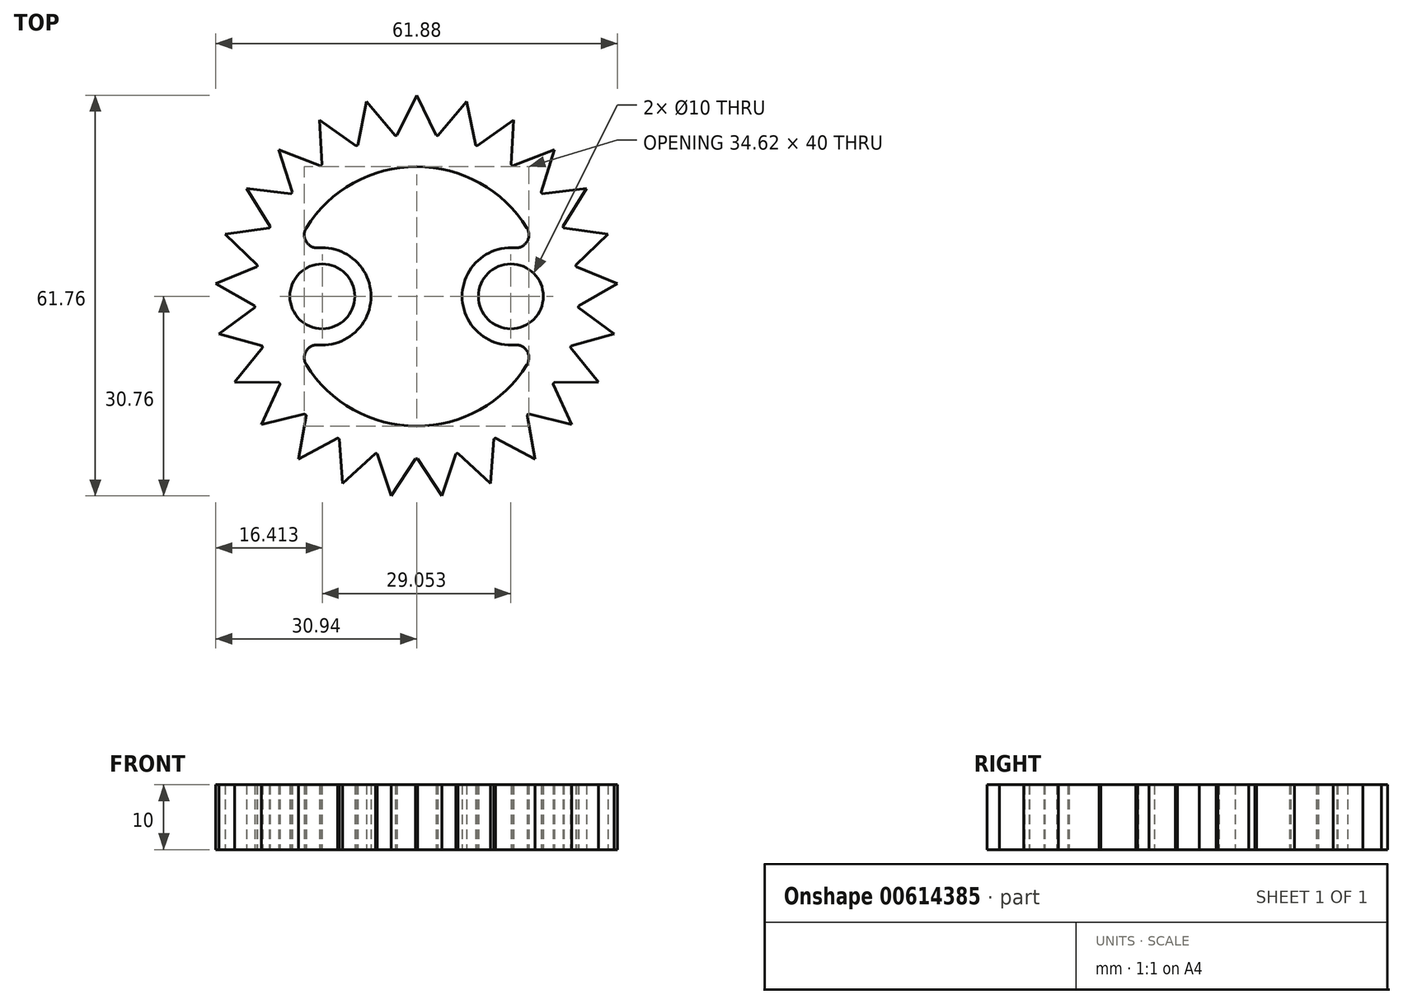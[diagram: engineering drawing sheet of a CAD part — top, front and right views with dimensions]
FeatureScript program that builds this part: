
annotation { "Feature Type Name" : "Feature", "Feature Type Description" : "" }
export const myFeature = defineFeature(function(context is Context, id is Id, definition is map)
    precondition{}
    {
        {
            var Q0;
            Q0=qCreatedBy(makeId("Top.planeOp"),FACE);
            var sketch = newSketch(context, id + "F0", { "sketchPlane" : qUnion([Q0])});
            skArc(sketch, "E0", {"start": v(-17, -10.52) * mm, "mid": v(0, -20) * mm, "end": v(17, -10.52) * mm});
            skArc(sketch, "E1", {"start": v(-14.59, 20.3) * mm, "mid": v(-14.7, 20.23) * mm, "end": v(-14.8, 20.15) * mm});
            skLineSegment(sketch, "E2", {"start": v(3, 24.82) * mm, "end": v(0, 31) * mm});
            skLineSegment(sketch, "E3", {"start": v(-3, 24.82) * mm, "end": v(0, 31) * mm});
            skLineSegment(sketch, "E4.1.0", {"start": v(-3.27, 24.79) * mm, "end": v(-7.7, 30.03) * mm});
            skLineSegment(sketch, "E4.1.1", {"start": v(-9.08, 23.3) * mm, "end": v(-7.7, 30.03) * mm});
            skLineSegment(sketch, "E4.2.0", {"start": v(-9.33, 23.2) * mm, "end": v(-14.93, 27.17) * mm});
            skLineSegment(sketch, "E4.2.1", {"start": v(-14.59, 20.3) * mm, "end": v(-14.93, 27.17) * mm});
            skLineSegment(sketch, "E4.3.0", {"start": v(-14.8, 20.15) * mm, "end": v(-21.22, 22.6) * mm});
            skLineSegment(sketch, "E4.3.1", {"start": v(-19.18, 16.04) * mm, "end": v(-21.22, 22.6) * mm});
            skLineSegment(sketch, "E4.4.0", {"start": v(-19.35, 15.83) * mm, "end": v(-26.17, 16.61) * mm});
            skLineSegment(sketch, "E4.4.1", {"start": v(-22.56, 10.77) * mm, "end": v(-26.17, 16.61) * mm});
            skLineSegment(sketch, "E4.5.0", {"start": v(-22.68, 10.52) * mm, "end": v(-29.48, 9.58) * mm});
            skLineSegment(sketch, "E4.5.1", {"start": v(-24.53, 4.82) * mm, "end": v(-29.48, 9.58) * mm});
            skLineSegment(sketch, "E4.6.0", {"start": v(-24.58, 4.55) * mm, "end": v(-30.94, 1.95) * mm});
            skLineSegment(sketch, "E4.6.1", {"start": v(-24.96, -1.44) * mm, "end": v(-30.94, 1.95) * mm});
            skLineSegment(sketch, "E4.7.0", {"start": v(-24.94, -1.7) * mm, "end": v(-30.45, -5.8) * mm});
            skLineSegment(sketch, "E4.7.1", {"start": v(-23.82, -7.6) * mm, "end": v(-30.45, -5.8) * mm});
            skLineSegment(sketch, "E4.8.0", {"start": v(-23.73, -7.85) * mm, "end": v(-28.05, -13.2) * mm});
            skLineSegment(sketch, "E4.8.1", {"start": v(-21.18, -13.28) * mm, "end": v(-28.05, -13.2) * mm});
            skLineSegment(sketch, "E4.9.0", {"start": v(-21.04, -13.5) * mm, "end": v(-23.89, -19.76) * mm});
            skLineSegment(sketch, "E4.9.1", {"start": v(-17.21, -18.13) * mm, "end": v(-23.89, -19.76) * mm});
            skLineSegment(sketch, "E4.10.0", {"start": v(-17.02, -18.32) * mm, "end": v(-18.22, -25.08) * mm});
            skLineSegment(sketch, "E4.10.1", {"start": v(-12.16, -21.84) * mm, "end": v(-18.22, -25.08) * mm});
            skLineSegment(sketch, "E4.11.0", {"start": v(-11.93, -21.97) * mm, "end": v(-11.41, -28.82) * mm});
            skLineSegment(sketch, "E4.11.1", {"start": v(-6.35, -24.18) * mm, "end": v(-11.41, -28.82) * mm});
            skLineSegment(sketch, "E4.12.0", {"start": v(-6.09, -24.25) * mm, "end": v(-3.89, -30.76) * mm});
            skLineSegment(sketch, "E4.12.1", {"start": v(-0.13, -25) * mm, "end": v(-3.89, -30.76) * mm});
            skLineSegment(sketch, "E4.13.0", {"start": v(0.13, -25) * mm, "end": v(3.89, -30.76) * mm});
            skLineSegment(sketch, "E4.13.1", {"start": v(6.09, -24.25) * mm, "end": v(3.89, -30.76) * mm});
            skLineSegment(sketch, "E4.14.0", {"start": v(6.35, -24.18) * mm, "end": v(11.41, -28.82) * mm});
            skLineSegment(sketch, "E4.14.1", {"start": v(11.93, -21.97) * mm, "end": v(11.41, -28.82) * mm});
            skLineSegment(sketch, "E4.15.0", {"start": v(12.16, -21.84) * mm, "end": v(18.22, -25.08) * mm});
            skLineSegment(sketch, "E4.15.1", {"start": v(17.02, -18.32) * mm, "end": v(18.22, -25.08) * mm});
            skLineSegment(sketch, "E4.16.0", {"start": v(17.21, -18.13) * mm, "end": v(23.89, -19.76) * mm});
            skLineSegment(sketch, "E4.16.1", {"start": v(21.04, -13.5) * mm, "end": v(23.89, -19.76) * mm});
            skLineSegment(sketch, "E4.17.0", {"start": v(21.18, -13.28) * mm, "end": v(28.05, -13.2) * mm});
            skLineSegment(sketch, "E4.17.1", {"start": v(23.73, -7.85) * mm, "end": v(28.05, -13.2) * mm});
            skLineSegment(sketch, "E4.18.0", {"start": v(23.82, -7.6) * mm, "end": v(30.45, -5.8) * mm});
            skLineSegment(sketch, "E4.18.1", {"start": v(24.94, -1.7) * mm, "end": v(30.45, -5.8) * mm});
            skLineSegment(sketch, "E4.19.0", {"start": v(24.96, -1.44) * mm, "end": v(30.94, 1.95) * mm});
            skLineSegment(sketch, "E4.19.1", {"start": v(24.58, 4.55) * mm, "end": v(30.94, 1.95) * mm});
            skLineSegment(sketch, "E4.20.0", {"start": v(24.53, 4.82) * mm, "end": v(29.48, 9.58) * mm});
            skLineSegment(sketch, "E4.20.1", {"start": v(22.68, 10.52) * mm, "end": v(29.48, 9.58) * mm});
            skLineSegment(sketch, "E4.21.0", {"start": v(22.56, 10.77) * mm, "end": v(26.17, 16.61) * mm});
            skLineSegment(sketch, "E4.21.1", {"start": v(19.35, 15.83) * mm, "end": v(26.17, 16.61) * mm});
            skLineSegment(sketch, "E4.22.0", {"start": v(19.18, 16.04) * mm, "end": v(21.22, 22.6) * mm});
            skLineSegment(sketch, "E4.22.1", {"start": v(14.8, 20.15) * mm, "end": v(21.22, 22.6) * mm});
            skLineSegment(sketch, "E4.23.0", {"start": v(14.59, 20.3) * mm, "end": v(14.93, 27.17) * mm});
            skLineSegment(sketch, "E4.23.1", {"start": v(9.33, 23.2) * mm, "end": v(14.93, 27.17) * mm});
            skLineSegment(sketch, "E4.24.0", {"start": v(9.08, 23.3) * mm, "end": v(7.7, 30.03) * mm});
            skLineSegment(sketch, "E4.24.1", {"start": v(3.27, 24.79) * mm, "end": v(7.7, 30.03) * mm});
            skCircle(sketch, "E5", {"center": v(-14.53, 0) * mm, "radius": 5 * mm});
            skArc(sketch, "E6", {"start": v(-15.14, -7.47) * mm, "mid": v(-7.03, 0) * mm, "end": v(-15.14, 7.47) * mm});
            skArc(sketch, "E7", {"start": v(-17, 10.52) * mm, "mid": v(-17.01, 8.42) * mm, "end": v(-15.14, 7.47) * mm});
            skArc(sketch, "E8", {"start": v(-15.14, -7.47) * mm, "mid": v(-17.01, -8.42) * mm, "end": v(-17, -10.52) * mm});
            skArc(sketch, "E9.1.0", {"start": v(17, -10.52) * mm, "mid": v(17.01, -8.42) * mm, "end": v(15.14, -7.47) * mm});
            skArc(sketch, "E9.1.1", {"start": v(15.14, 7.47) * mm, "mid": v(7.03, 0) * mm, "end": v(15.14, -7.47) * mm});
            skCircle(sketch, "E9.1.2", {"center": v(14.53, 0) * mm, "radius": 5 * mm});
            skArc(sketch, "E9.1.3", {"start": v(15.14, 7.47) * mm, "mid": v(17.01, 8.42) * mm, "end": v(17, 10.52) * mm});
            skArc(sketch, "E10.trimOffspring", {"start": v(-9.08, 23.3) * mm, "mid": v(-9.2, 23.24) * mm, "end": v(-9.33, 23.2) * mm});
            skArc(sketch, "E11.trimOffspring", {"start": v(-3, 24.82) * mm, "mid": v(-3.13, 24.8) * mm, "end": v(-3.27, 24.79) * mm});
            skArc(sketch, "E12.trimOffspring", {"start": v(3.27, 24.79) * mm, "mid": v(3.13, 24.8) * mm, "end": v(3, 24.82) * mm});
            skArc(sketch, "E13.trimOffspring", {"start": v(9.33, 23.2) * mm, "mid": v(9.2, 23.24) * mm, "end": v(9.08, 23.3) * mm});
            skArc(sketch, "E14.trimOffspring", {"start": v(14.8, 20.15) * mm, "mid": v(14.7, 20.23) * mm, "end": v(14.59, 20.3) * mm});
            skArc(sketch, "E15.trimOffspring", {"start": v(19.35, 15.83) * mm, "mid": v(19.26, 15.94) * mm, "end": v(19.18, 16.04) * mm});
            skArc(sketch, "E16.trimOffspring", {"start": v(22.68, 10.52) * mm, "mid": v(22.62, 10.64) * mm, "end": v(22.56, 10.77) * mm});
            skArc(sketch, "E17.trimOffspring", {"start": v(24.58, 4.55) * mm, "mid": v(24.56, 4.68) * mm, "end": v(24.53, 4.82) * mm});
            skArc(sketch, "E18.trimOffspring", {"start": v(24.94, -1.7) * mm, "mid": v(24.95, -1.57) * mm, "end": v(24.96, -1.44) * mm});
            skArc(sketch, "E19.trimOffspring", {"start": v(23.73, -7.85) * mm, "mid": v(23.78, -7.73) * mm, "end": v(23.82, -7.6) * mm});
            skArc(sketch, "E20.trimOffspring", {"start": v(17.02, -18.32) * mm, "mid": v(17.11, -18.22) * mm, "end": v(17.21, -18.13) * mm});
            skArc(sketch, "E21.trimOffspring", {"start": v(21.04, -13.5) * mm, "mid": v(21.1, -13.4) * mm, "end": v(21.18, -13.28) * mm});
            skArc(sketch, "E22.trimOffspring", {"start": v(11.93, -21.97) * mm, "mid": v(12.04, -21.9) * mm, "end": v(12.16, -21.84) * mm});
            skArc(sketch, "E23.trimOffspring", {"start": v(6.09, -24.25) * mm, "mid": v(6.22, -24.21) * mm, "end": v(6.35, -24.18) * mm});
            skArc(sketch, "E24.trimOffspring", {"start": v(-0.13, -25) * mm, "mid": v(0, -25) * mm, "end": v(0.13, -25) * mm});
            skArc(sketch, "E25.trimOffspring", {"start": v(-6.35, -24.18) * mm, "mid": v(-6.22, -24.21) * mm, "end": v(-6.09, -24.25) * mm});
            skArc(sketch, "E26.trimOffspring", {"start": v(-12.16, -21.84) * mm, "mid": v(-12.04, -21.9) * mm, "end": v(-11.93, -21.97) * mm});
            skArc(sketch, "E27.trimOffspring", {"start": v(-17.21, -18.13) * mm, "mid": v(-17.11, -18.22) * mm, "end": v(-17.02, -18.32) * mm});
            skArc(sketch, "E28.trimOffspring", {"start": v(-21.18, -13.28) * mm, "mid": v(-21.1, -13.4) * mm, "end": v(-21.04, -13.5) * mm});
            skArc(sketch, "E29.trimOffspring", {"start": v(-23.82, -7.6) * mm, "mid": v(-23.78, -7.73) * mm, "end": v(-23.73, -7.85) * mm});
            skArc(sketch, "E30.trimOffspring", {"start": v(-24.96, -1.44) * mm, "mid": v(-24.95, -1.57) * mm, "end": v(-24.94, -1.7) * mm});
            skArc(sketch, "E31.trimOffspring", {"start": v(-24.53, 4.82) * mm, "mid": v(-24.56, 4.68) * mm, "end": v(-24.58, 4.55) * mm});
            skArc(sketch, "E32.trimOffspring", {"start": v(-22.56, 10.77) * mm, "mid": v(-22.62, 10.64) * mm, "end": v(-22.68, 10.52) * mm});
            skArc(sketch, "E33.trimOffspring", {"start": v(-19.18, 16.04) * mm, "mid": v(-19.26, 15.94) * mm, "end": v(-19.35, 15.83) * mm});
            skArc(sketch, "E34.trimOffspring", {"start": v(17, 10.52) * mm, "mid": v(0, 20) * mm, "end": v(-17, 10.52) * mm});
            skSolve(sketch);
        }
        {
            var Q0;
            Q0=makeQuery(id+"F0.imprint","IMPRINT",FACE,{"disambiguationData":[TD([[makeQuery(id+"F0.imprint","IMPRINT",EDGE,{"derivedFrom":sQuery(id+"F0.wireOp",EDGE,"E0")}),-1.0]])]});
            extrude(context, id + "F1", {"entities" : qUnion([Q0]), "depth" : 10 * mm, "offsetDistance" : 25 * mm});
        }
    });
